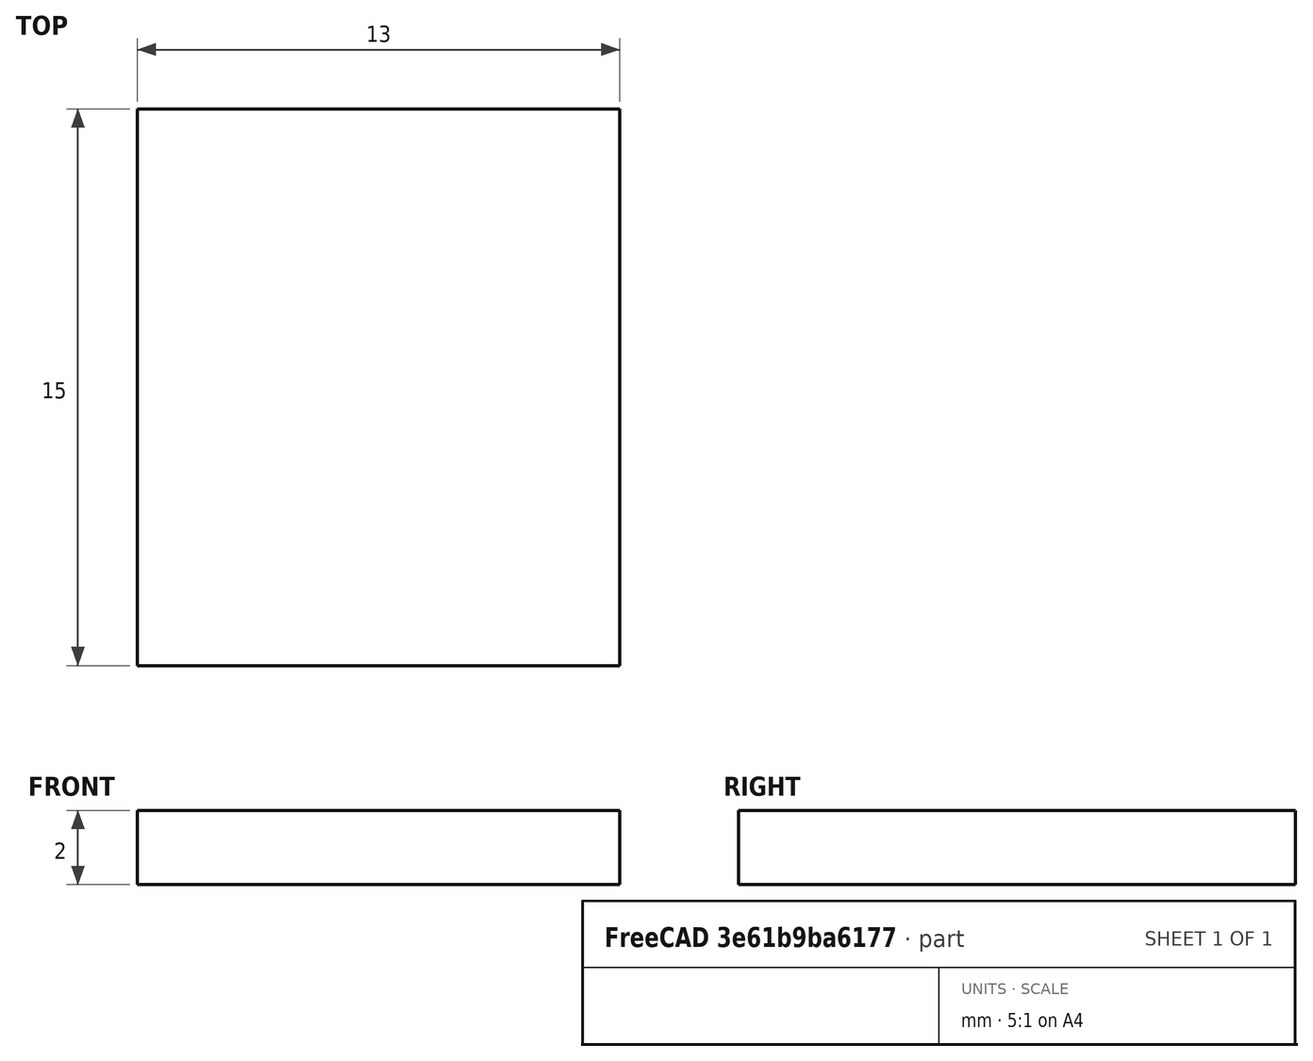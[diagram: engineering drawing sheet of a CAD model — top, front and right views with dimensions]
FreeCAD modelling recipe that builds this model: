
FCSTD DOCUMENT  (FreeCAD 0.16R6712 (Git))
Label: BGM111A256V2
License: All rights reserved
LicenseURL: http://en.wikipedia.org/wiki/All_rights_reserved
objects: Sketcher::SketchObject×1, Part::Feature×1
note: 2 computed .brp shape members not serialized (recipe doc carries the construction recipe); baked Part::Feature solids carry a one-line shape summary decoded from their .brp

FEATURE [Sketcher::SketchObject] Sketch
  sketch-geometry (4):
    g0: LineSegment StartX=-6.5 StartY=-7.5 StartZ=0 EndX=6.5 EndY=-7.5 EndZ=0
    g1: LineSegment StartX=6.5 StartY=-7.5 StartZ=0 EndX=6.5 EndY=7.5 EndZ=0
    g2: LineSegment StartX=6.5 StartY=7.5 StartZ=0 EndX=-6.5 EndY=7.5 EndZ=0
    g3: LineSegment StartX=-6.5 StartY=7.5 StartZ=0 EndX=-6.5 EndY=-7.5 EndZ=0
  constraints (8):
    c: Coincident(g0,g1)
    c: Coincident(g1,g2)
    c: Coincident(g2,g3)
    c: Coincident(g3,g0)
    c: Horizontal(g0)
    c: Horizontal(g2)
    c: Vertical(g1)
    c: Vertical(g3)
FEATURE [Part::Feature] Shape  label="Pad"
  shape: bbox 13 x 15 x 2 mm, 6 faces (baked)
